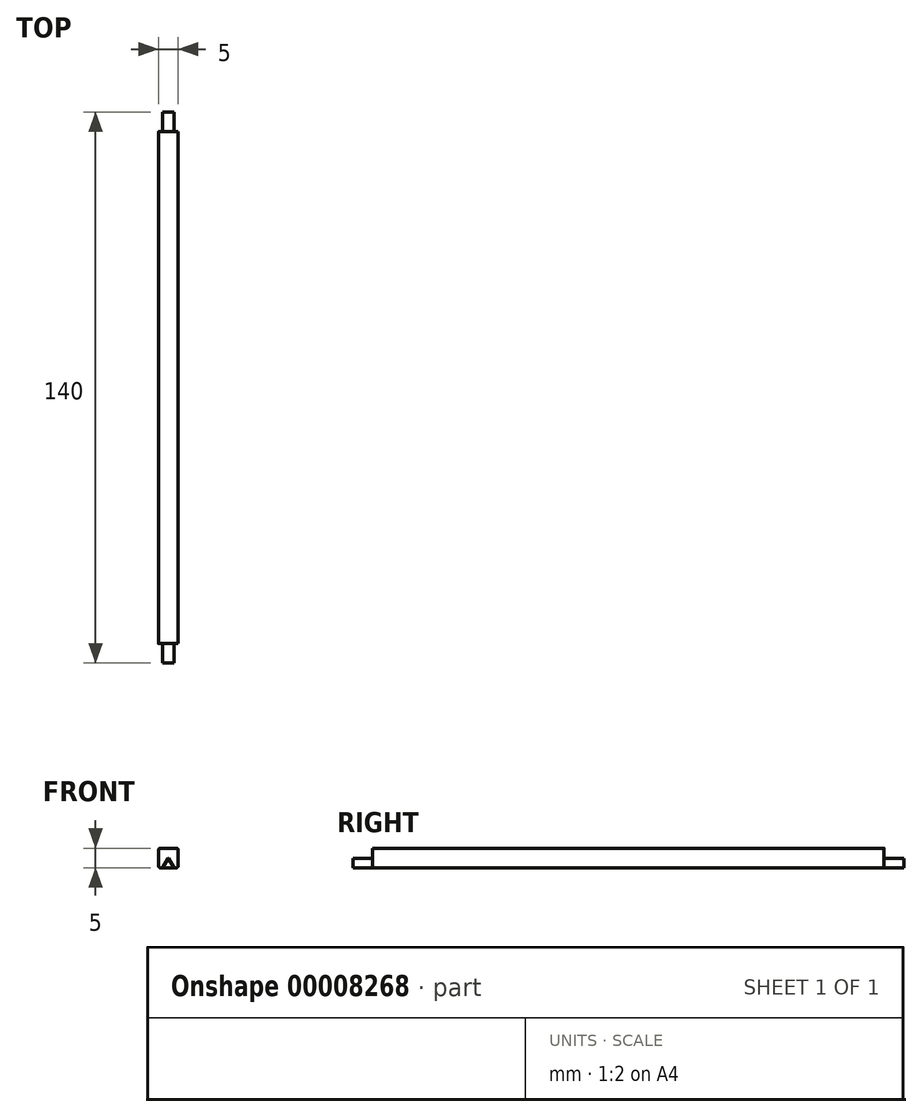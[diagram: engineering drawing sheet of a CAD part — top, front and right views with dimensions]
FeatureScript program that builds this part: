
annotation { "Feature Type Name" : "Feature", "Feature Type Description" : "" }
export const myFeature = defineFeature(function(context is Context, id is Id, definition is map)
    precondition{}
    {
        {
            var Q0;
            Q0=qCreatedBy(makeId("Top.planeOp"),FACE);
            var sketch = newSketch(context, id + "F0", { "sketchPlane" : qUnion([Q0])});
            skLineSegment(sketch, "E0.bottom", {"start": v(-34.8, 119.92) * mm, "end": v(-29.8, 119.92) * mm});
            skLineSegment(sketch, "E0.top", {"start": v(-34.8, -20.08) * mm, "end": v(-29.8, -20.08) * mm});
            skLineSegment(sketch, "E0.left", {"start": v(-34.8, 119.92) * mm, "end": v(-34.8, -20.08) * mm});
            skLineSegment(sketch, "E0.right", {"start": v(-29.8, 119.92) * mm, "end": v(-29.8, -20.08) * mm});
            skSolve(sketch);
        }
        {
            var Q0;
            Q0 = qSketchRegion(id + "F0", true);
            extrude(context, id + "F1", {"entities" : qUnion([Q0]), "depth" : 5 * mm});
        }
        {
            var Q0;
            Q0=makeQuery(id+"F1.opExtrude","SWEPT_FACE",FACE,{"disambiguationData":[OSD([sQuery(id+"F0.wireOp",EDGE,"E0.top")])]});
            var sketch = newSketch(context, id + "F2", { "sketchPlane" : qUnion([Q0])});
            skLineSegment(sketch, "E1", {"start": v(-30.84, 0) * mm, "end": v(-32.3, 2.51) * mm});
            skLineSegment(sketch, "E2", {"start": v(-32.3, 2.51) * mm, "end": v(-33.74, 0) * mm});
            skLineSegment(sketch, "E3", {"start": v(-32.3, 2.51) * mm, "end": v(-29.8, 2.51) * mm, "construction": true});
            skLineSegment(sketch, "E4", {"start": v(-32.3, 2.51) * mm, "end": v(-34.8, 2.51) * mm, "construction": true});
            skLineSegment(sketch, "E5.bottom", {"start": v(-34.8, 5) * mm, "end": v(-29.8, 5) * mm});
            skLineSegment(sketch, "E5.top", {"start": v(-34.8, 0) * mm, "end": v(-33.74, 0) * mm});
            skLineSegment(sketch, "E5.left", {"start": v(-34.8, 5) * mm, "end": v(-34.8, 0) * mm});
            skLineSegment(sketch, "E5.right", {"start": v(-29.8, 5) * mm, "end": v(-29.8, 0) * mm});
            skLineSegment(sketch, "E6.trimOffspring", {"start": v(-30.84, 0) * mm, "end": v(-29.8, 0) * mm});
            skSolve(sketch);
        }
        {
            var Q0;
            Q0 = qSketchRegion(id + "F2", true);
            extrude(context, id + "F3", {"entities" : qUnion([Q0]), "operationType" : NewBodyOperationType.REMOVE, "oppositeDirection" : true, "depth" : 5 * mm});
        }
        {
            var Q0;
            Q0=makeQuery(id+"F1.opExtrude","SWEPT_FACE",FACE,{"disambiguationData":[OSD([sQuery(id+"F0.wireOp",EDGE,"E0.bottom")])]});
            var sketch = newSketch(context, id + "F4", { "sketchPlane" : qUnion([Q0])});
            skLineSegment(sketch, "E7", {"start": v(32.3, 2.51) * mm, "end": v(33.74, 0) * mm});
            skLineSegment(sketch, "E8", {"start": v(30.84, 0) * mm, "end": v(32.3, 2.51) * mm});
            skLineSegment(sketch, "E9.bottom", {"start": v(29.8, 5) * mm, "end": v(34.8, 5) * mm});
            skLineSegment(sketch, "E9.top", {"start": v(29.8, 0) * mm, "end": v(30.84, 0) * mm});
            skLineSegment(sketch, "E9.left", {"start": v(29.8, 5) * mm, "end": v(29.8, 0) * mm});
            skLineSegment(sketch, "E9.right", {"start": v(34.8, 5) * mm, "end": v(34.8, 0) * mm});
            skLineSegment(sketch, "E10.trimOffspring", {"start": v(33.74, 0) * mm, "end": v(34.8, 0) * mm});
            skSolve(sketch);
        }
        {
            var Q0;
            Q0 = qSketchRegion(id + "F4", true);
            extrude(context, id + "F5", {"entities" : qUnion([Q0]), "operationType" : NewBodyOperationType.REMOVE, "oppositeDirection" : true, "depth" : 5 * mm});
        }
        {
            var Q0;
            Q0=makeQuery(id+"F3.boolean.opBoolean","COPY",EDGE,{"derivedFrom":makeQuery(id+"F3.opExtrude","SWEPT_EDGE",EDGE,{"disambiguationData":[OSD([sQuery(id+"F2.wireOp",EDGE,"E1"),sQuery(id+"F2.wireOp",EDGE,"E2")])]})});
            var Q1;
            Q1=makeQuery(id+"F3.boolean.opBoolean","COPY",EDGE,{"derivedFrom":makeQuery(id+"F3.opExtrude","SWEPT_EDGE",EDGE,{"disambiguationData":[OSD([sQuery(id+"F0.wireOp",EDGE,"E0.top"),sQuery(id+"F2.wireOp",EDGE,"E1"),sQuery(id+"F2.wireOp",EDGE,"E6.trimOffspring")])]})});
            var Q2;
            Q2=makeQuery(id+"F3.boolean.opBoolean","COPY",EDGE,{"derivedFrom":makeQuery(id+"F3.opExtrude","SWEPT_EDGE",EDGE,{"disambiguationData":[OSD([sQuery(id+"F0.wireOp",EDGE,"E0.top"),sQuery(id+"F2.wireOp",EDGE,"E2"),sQuery(id+"F2.wireOp",EDGE,"E5.top")])]})});
            var Q3;
            Q3=makeQuery(id+"F5.boolean.opBoolean","COPY",EDGE,{"derivedFrom":makeQuery(id+"F5.opExtrude","SWEPT_EDGE",EDGE,{"disambiguationData":[OSD([sQuery(id+"F4.wireOp",EDGE,"E7"),sQuery(id+"F4.wireOp",EDGE,"E8")])]})});
            var Q4;
            Q4=makeQuery(id+"F5.boolean.opBoolean","COPY",EDGE,{"derivedFrom":makeQuery(id+"F5.opExtrude","SWEPT_EDGE",EDGE,{"disambiguationData":[OSD([sQuery(id+"F0.wireOp",EDGE,"E0.bottom"),sQuery(id+"F4.wireOp",EDGE,"E7"),sQuery(id+"F4.wireOp",EDGE,"E10.trimOffspring")])]})});
            var Q5;
            Q5=makeQuery(id+"F5.boolean.opBoolean","COPY",EDGE,{"derivedFrom":makeQuery(id+"F5.opExtrude","SWEPT_EDGE",EDGE,{"disambiguationData":[OSD([sQuery(id+"F0.wireOp",EDGE,"E0.bottom"),sQuery(id+"F4.wireOp",EDGE,"E8"),sQuery(id+"F4.wireOp",EDGE,"E9.top")])]})});
            fillet(context, id + "F6", {"entities" : qUnion([Q0, Q1, Q2, Q3, Q4, Q5]), "radius" : 0.1 * mm, "tangentPropagation" : true, "allowEdgeOverflow" : false});
        }
        {
            var Q0;
            Q0=makeQuery(id+"F1.opExtrude","CAP_EDGE",EDGE,{"disambiguationData":[OSD([sQuery(id+"F0.wireOp",EDGE,"E0.left")])],"isStart":false});
            var Q1;
            Q1=makeQuery(id+"F1.opExtrude","CAP_EDGE",EDGE,{"disambiguationData":[OSD([sQuery(id+"F0.wireOp",EDGE,"E0.right")])],"isStart":false});
            var Q2;
            Q2=makeQuery(id+"F1.opExtrude","CAP_EDGE",EDGE,{"disambiguationData":[OSD([sQuery(id+"F0.wireOp",EDGE,"E0.right")])],"isStart":true});
            var Q3;
            Q3=makeQuery(id+"F1.opExtrude","CAP_EDGE",EDGE,{"disambiguationData":[OSD([sQuery(id+"F0.wireOp",EDGE,"E0.left")])],"isStart":true});
            fillet(context, id + "F7", {"entities" : qUnion([Q0, Q1, Q2, Q3]), "radius" : 0.5 * mm, "tangentPropagation" : true, "allowEdgeOverflow" : false});
        }
    });
